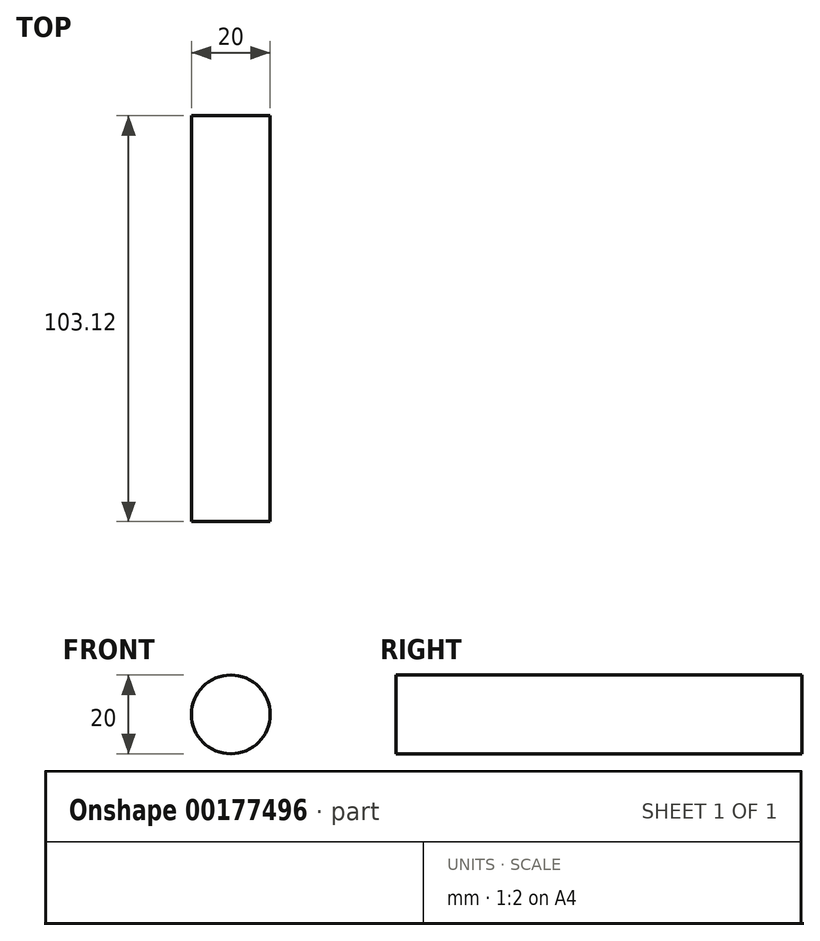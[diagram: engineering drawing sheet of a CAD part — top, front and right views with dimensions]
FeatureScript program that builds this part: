
annotation { "Feature Type Name" : "Feature", "Feature Type Description" : "" }
export const myFeature = defineFeature(function(context is Context, id is Id, definition is map)
    precondition{}
    {
        {
            var Q0;
            Q0=qCreatedBy(makeId("Front.planeOp"),FACE);
            var sketch = newSketch(context, id + "F0", { "sketchPlane" : qUnion([Q0])});
            skCircle(sketch, "E0", {"center": v(0, 0) * mm, "radius": 10 * mm});
            skSolve(sketch);
        }
        {
            var Q0;
            Q0 = qSketchRegion(id + "F0", true);
            extrude(context, id + "F1", {"entities" : qUnion([Q0]), "depth" : 103.12 * mm});
        }
    });
